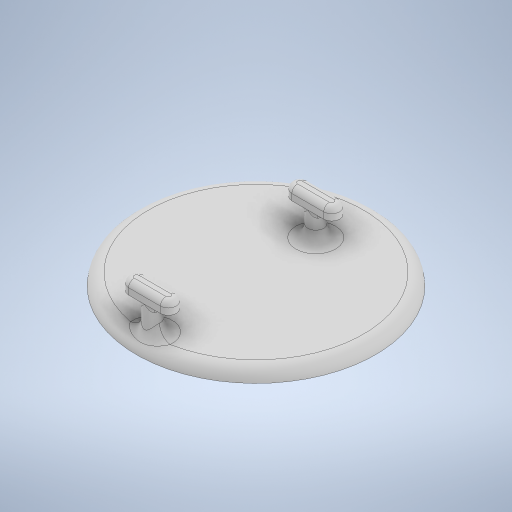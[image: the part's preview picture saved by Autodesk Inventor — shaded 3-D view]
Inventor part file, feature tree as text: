
AUTODESK INVENTOR PART (.ipt)
format: ipt  version: 2023 (Build 270158000, 158)  size: 841,216 bytes
history: native  units: mm
features: sketch x6, extrude x6, fillet x5, chamfer x2, other x1
ambient origin geometry x8: Origin, YZ Plane, XZ Plane, XY Plane, X Axis, Y Axis, Z Axis, Center Point
bodies: Body1 (feature_tree)
feature tree (20):
  other  "Bryła1"
  sketch  "Szkic1"
  extrude  "Wyciągnięcie proste1"  Depth=60.0mm
  sketch  "Szkic2"
  extrude  "Wyciągnięcie proste2"  Depth=4.0mm
  sketch  "Szkic3"
  extrude  "Wyciągnięcie proste3"  Depth=4.0mm
  extrude  "Wyciągnięcie proste4"  Depth=3.0mm TaperAngle=0.0deg
  chamfer  "Faza1"  Distance=10.0mm
  chamfer  "Faza2"  Distance=5.0mm
  sketch  "Szkic4"
  fillet  "Zaokrąglenie1"  Radius=32.0mm
  fillet  "Zaokrąglenie2"  Radius=8.0mm
  extrude  "Wyciągnięcie proste5"  Depth=2.0mm TaperAngle=0.0deg
  extrude  "Wyciągnięcie proste6"  Depth=2.5mm TaperAngle=0.0deg
  fillet  "Zaokrąglenie3"  Radius=2.0mm
  fillet  "Zaokrąglenie4"  Radius=2.0mm
  fillet  "Zaokrąglenie5"  Radius=1.0mm
  sketch  "Szkic5"
  sketch  "Szkic6"
